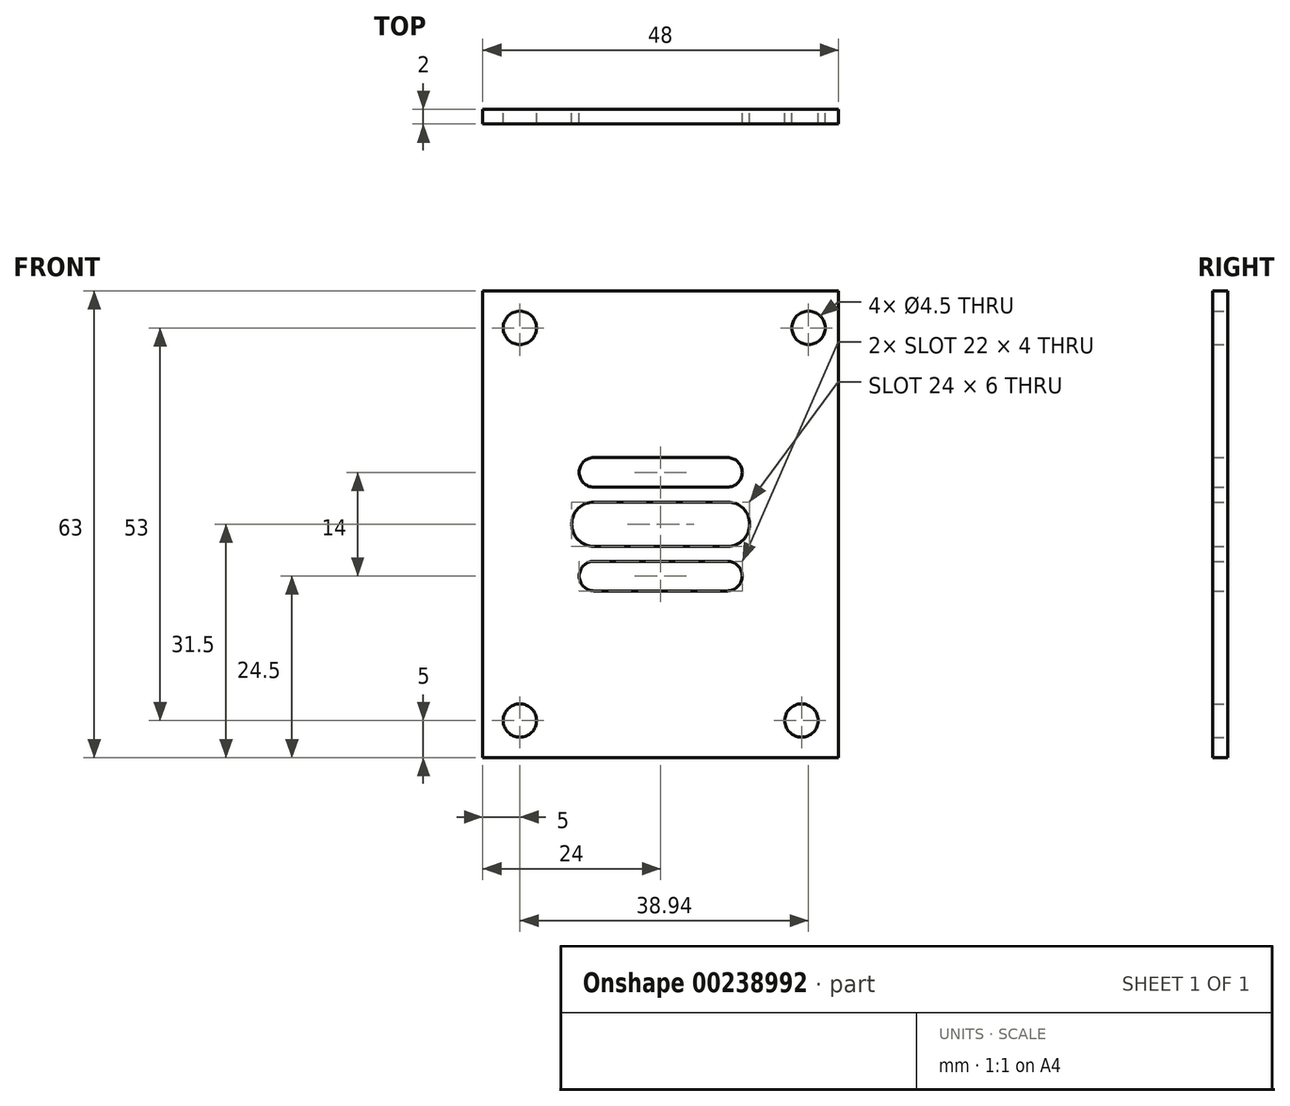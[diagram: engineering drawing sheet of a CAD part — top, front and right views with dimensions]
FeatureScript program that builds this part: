
annotation { "Feature Type Name" : "Feature", "Feature Type Description" : "" }
export const myFeature = defineFeature(function(context is Context, id is Id, definition is map)
    precondition{}
    {
        {
            var Q0;
            Q0=qCreatedBy(makeId("Front.planeOp"),FACE);
            var sketch = newSketch(context, id + "F0", { "sketchPlane" : qUnion([Q0])});
            skLineSegment(sketch, "E0.bottom", {"start": v(0, 0) * mm, "end": v(48, 0) * mm});
            skLineSegment(sketch, "E0.top", {"start": v(0, 63) * mm, "end": v(48, 63) * mm});
            skLineSegment(sketch, "E0.left", {"start": v(0, 0) * mm, "end": v(0, 63) * mm});
            skLineSegment(sketch, "E0.right", {"start": v(48, 0) * mm, "end": v(48, 63) * mm});
            skCircle(sketch, "E1", {"center": v(5, 5) * mm, "radius": 2.25 * mm});
            skCircle(sketch, "E2", {"center": v(43, 5) * mm, "radius": 2.25 * mm});
            skCircle(sketch, "E3", {"center": v(43.94, 58) * mm, "radius": 2.25 * mm});
            skCircle(sketch, "E4", {"center": v(5, 58) * mm, "radius": 2.25 * mm});
            skArc(sketch, "E5", {"start": v(15, 34.5) * mm, "mid": v(12, 31.5) * mm, "end": v(15, 28.5) * mm});
            skArc(sketch, "E6", {"start": v(33, 28.5) * mm, "mid": v(36, 31.5) * mm, "end": v(33, 34.5) * mm});
            skLineSegment(sketch, "E7", {"start": v(15, 34.5) * mm, "end": v(33, 34.5) * mm});
            skLineSegment(sketch, "E8", {"start": v(15, 28.5) * mm, "end": v(33, 28.5) * mm});
            skArc(sketch, "E9", {"start": v(15, 40.5) * mm, "mid": v(13, 38.5) * mm, "end": v(15, 36.5) * mm});
            skArc(sketch, "E10", {"start": v(15, 26.5) * mm, "mid": v(13, 24.5) * mm, "end": v(15, 22.5) * mm});
            skArc(sketch, "E11.MirrorC", {"start": v(33, 40.5) * mm, "mid": v(35, 38.5) * mm, "end": v(33, 36.5) * mm});
            skArc(sketch, "E12.MirrorC", {"start": v(33, 26.5) * mm, "mid": v(35, 24.5) * mm, "end": v(33, 22.5) * mm});
            skLineSegment(sketch, "E13", {"start": v(15, 40.5) * mm, "end": v(33, 40.5) * mm});
            skLineSegment(sketch, "E14", {"start": v(15, 36.5) * mm, "end": v(33, 36.5) * mm});
            skLineSegment(sketch, "E15.MirrorCS", {"start": v(15, 26.5) * mm, "end": v(33, 26.5) * mm});
            skLineSegment(sketch, "E16.MirrorCS", {"start": v(15, 22.5) * mm, "end": v(33, 22.5) * mm});
            skSolve(sketch);
        }
        {
            var Q0;
            Q0 = qSketchRegion(id + "F0", true);
            extrude(context, id + "F1", {"entities" : qUnion([Q0]), "depth" : 2 * mm});
        }
    });
